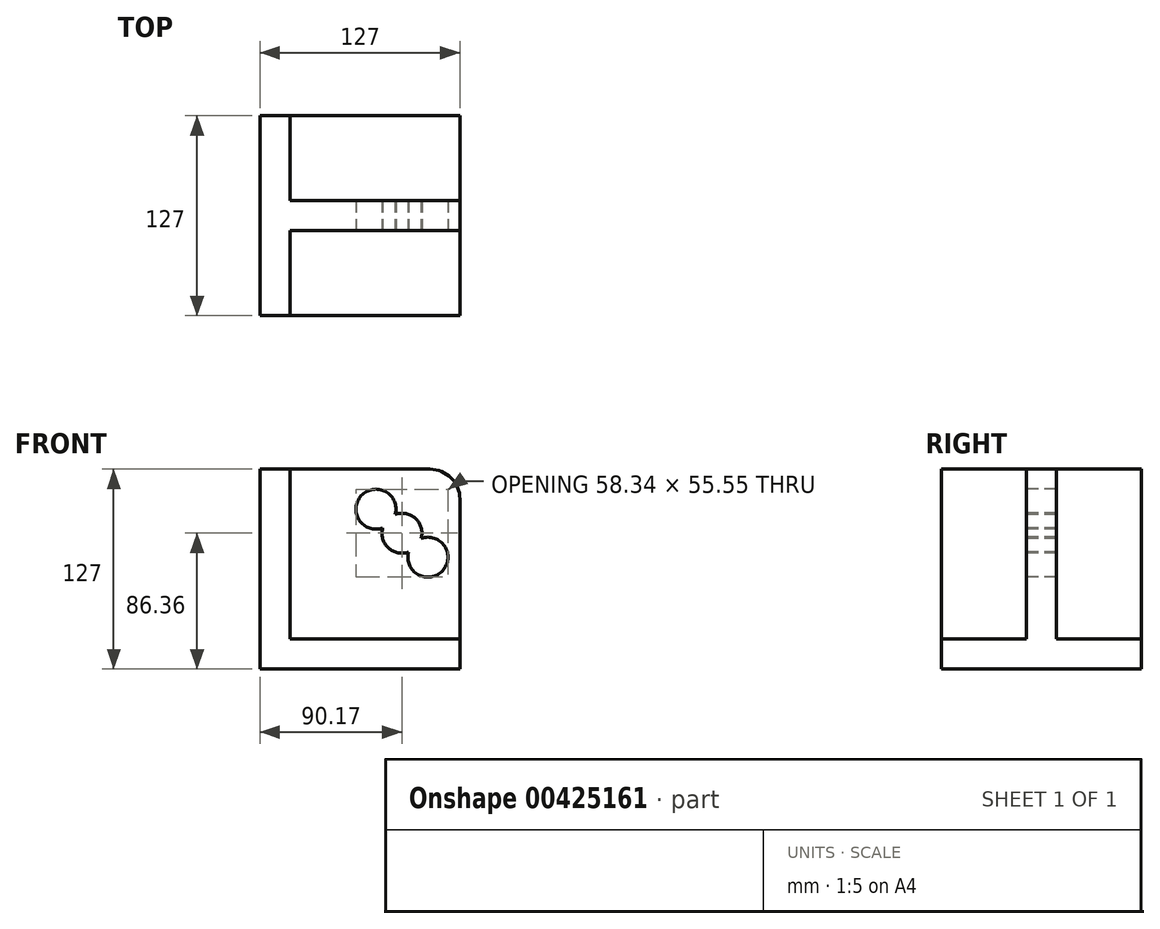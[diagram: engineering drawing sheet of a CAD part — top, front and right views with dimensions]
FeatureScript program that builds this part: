
annotation { "Feature Type Name" : "Feature", "Feature Type Description" : "" }
export const myFeature = defineFeature(function(context is Context, id is Id, definition is map)
    precondition{}
    {
        {
            var Q0;
            Q0=qCreatedBy(makeId("Front.planeOp"),FACE);
            var sketch = newSketch(context, id + "F0", { "sketchPlane" : qUnion([Q0])});
            skLineSegment(sketch, "E0", {"start": v(0, 0) * mm, "end": v(0, 127) * mm});
            skLineSegment(sketch, "E1", {"start": v(0, 0) * mm, "end": v(127, 0) * mm});
            skLineSegment(sketch, "E2", {"start": v(127, 0) * mm, "end": v(127, 19.05) * mm});
            skLineSegment(sketch, "E3", {"start": v(0, 127) * mm, "end": v(19.05, 127) * mm});
            skLineSegment(sketch, "E4", {"start": v(19.05, 127) * mm, "end": v(19.05, 19.05) * mm});
            skLineSegment(sketch, "E5", {"start": v(19.05, 19.05) * mm, "end": v(127, 19.05) * mm});
            skSolve(sketch);
        }
        {
            var Q0;
            Q0 = qSketchRegion(id + "F0", true);
            extrude(context, id + "F1", {"entities" : qUnion([Q0]), "depth" : 127 * mm});
        }
        {
            var Q0;
            Q0=makeQuery(id+"F1.opExtrude","SWEPT_FACE",FACE,{"disambiguationData":[OSD([sQuery(id+"F0.wireOp",EDGE,"E4")])]});
            var sketch = newSketch(context, id + "F2", { "sketchPlane" : qUnion([Q0])});
            skLineSegment(sketch, "E6.bottom", {"start": v(-73.03, 127) * mm, "end": v(-53.98, 127) * mm});
            skLineSegment(sketch, "E6.top", {"start": v(-73.03, 19.05) * mm, "end": v(-53.98, 19.05) * mm});
            skLineSegment(sketch, "E6.left", {"start": v(-73.03, 127) * mm, "end": v(-73.03, 19.05) * mm});
            skLineSegment(sketch, "E6.right", {"start": v(-53.98, 127) * mm, "end": v(-53.98, 19.05) * mm});
            skSolve(sketch);
        }
        {
            var Q0;
            Q0 = qSketchRegion(id + "F2", true);
            var Q1;
            Q1=makeQuery(id+"F1.opExtrude","SWEPT_FACE",FACE,{"disambiguationData":[OSD([sQuery(id+"F0.wireOp",EDGE,"E2")])]});
            extrude(context, id + "F3", {"entities" : qUnion([Q0]), "operationType" : NewBodyOperationType.ADD, "endBound" : BoundingType.UP_TO_SURFACE, "endBoundEntityFace" : qUnion([Q1]), "depth" : 25.4 * mm});
        }
        {
            var Q0;
            Q0=makeQuery(id+"F3.opExtrude","CAP_EDGE",EDGE,{"disambiguationData":[OSD([sQuery(id+"F2.wireOp",EDGE,"E6.bottom")])],"isStart":false});
            fillet(context, id + "F4", {"entities" : qUnion([Q0]), "radius" : 19.05 * mm, "tangentPropagation" : true, "allowEdgeOverflow" : false});
        }
        {
            var Q0;
            Q0=makeQuery(id+"F3.opExtrude","SWEPT_FACE",FACE,{"disambiguationData":[OSD([sQuery(id+"F2.wireOp",EDGE,"E6.left")])]});
            var sketch = newSketch(context, id + "F5", { "sketchPlane" : qUnion([Q0])});
            skArc(sketch, "E7", {"start": v(94.4, 74.39) * mm, "mid": v(116.01, 62.5) * mm, "end": v(102.44, 83.1) * mm});
            skArc(sketch, "E8", {"start": v(85.93, 98.33) * mm, "mid": v(64.33, 110.21) * mm, "end": v(77.9, 89.63) * mm});
            skLineSegment(sketch, "E9", {"start": v(73.66, 101.6) * mm, "end": v(106.68, 71.12) * mm, "construction": true});
            skArc(sketch, "E10", {"start": v(77.9, 89.63) * mm, "mid": v(81.56, 77.03) * mm, "end": v(94.4, 74.39) * mm});
            skArc(sketch, "E11.trimOffspring", {"start": v(102.44, 83.1) * mm, "mid": v(98.78, 95.7) * mm, "end": v(85.93, 98.33) * mm});
            skSolve(sketch);
        }
        {
            var Q0;
            Q0 = qSketchRegion(id + "F5", true);
            extrude(context, id + "F6", {"entities" : qUnion([Q0]), "operationType" : NewBodyOperationType.REMOVE, "oppositeDirection" : true, "depth" : 25.4 * mm});
        }
    });
